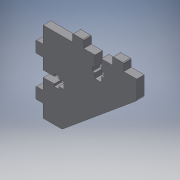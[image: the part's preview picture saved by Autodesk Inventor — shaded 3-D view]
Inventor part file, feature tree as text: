
AUTODESK INVENTOR PART (.ipt)
format: ipt  version: 2019 (Build 230136000, 136)  size: 267,776 bytes
history: native  units: in
note: dims shown in document units (in); Inventor stores cm internally (conversion verified against a paired STEP export)
features: reference x6, extrude x5, sketch x5, other x5, fillet x2, projected_geometry x1, helix x1
ambient origin geometry x8: Origin, YZ Plane, XZ Plane, XY Plane, X Axis, Y Axis, Z Axis, Center Point
bodies: Solid1 (feature_tree)
feature tree (25):
  extrude  "Extrusion1"  Depth=0.3937in
  fillet  "Fillet1"  Radius=0.1575in
  extrude  "Extrusion2"  Depth=0.1575in TaperAngle=0.0deg
  extrude  "Extrusion3"  Depth=0.1575in
  extrude  "Extrusion4"  Depth=1.0in TaperAngle=0.0deg
  extrude  "Extrusion5"  Depth=0.0197in
  fillet  "Fillet2"  [1 undecoded]
  sketch  "Sketch1"  dims[d0=0.3937in d1=0.3937in d2=0.1575in d3=0.0in]
  reference  "Reference1"
  sketch  "Sketch2"  dims[d4=0.0787in d5=0.1575in d6=0.0in]
  reference  "Reference3"
  reference  "Reference4"
  sketch  "Sketch3"  dims[d7=0.1575in d8=0.0in d9=0.0079in]
  reference  "Reference5"
  reference  "Reference6"
  reference  "Reference7"
  sketch  "Sketch4"  dims[d10=0.0079in d11=1.0in d12=0.0in]
  projected_geometry  "Projected Loop1"
  sketch  "Sketch5"  dims[d13=1.0in d14=0.0in d15=0.0197in]
  other  "<userpath>\Documents\CAD Files\Helix DLP\Helix DLP.iam"
  helix  "Helix DLP.iam"  [1 undecoded]
  other  "Motor Brace_1:1"
  other  "Maker_jigsaw_template:2"
  other  "Maker_jigsaw_template:3"
  other  "Motor_brace_2:1"
note: 2 required parameter values undecoded (feature->parameter linkage not recoverable at this tier; creation-order binding heuristic only, values carry confidence <= 0.55)
